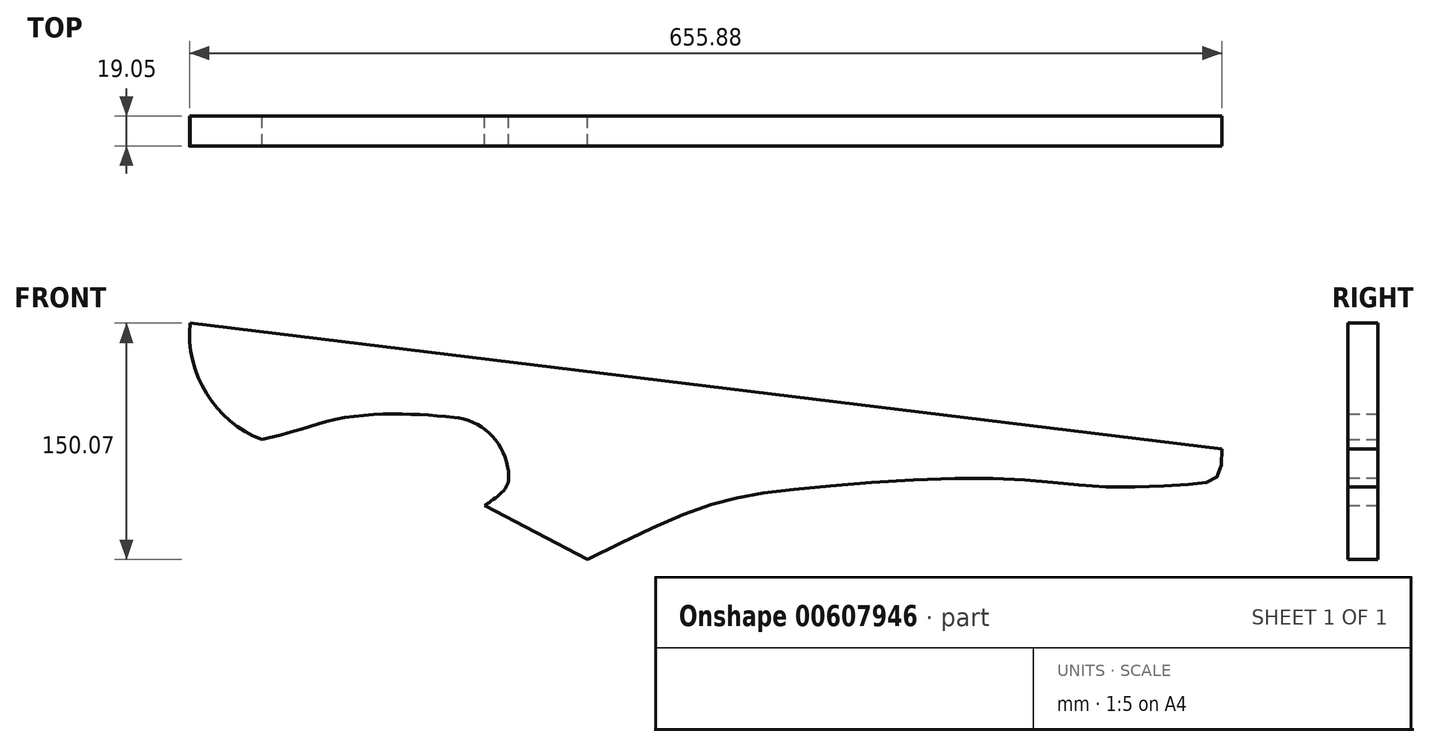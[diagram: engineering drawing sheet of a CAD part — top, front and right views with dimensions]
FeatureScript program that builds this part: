
annotation { "Feature Type Name" : "Feature", "Feature Type Description" : "" }
export const myFeature = defineFeature(function(context is Context, id is Id, definition is map)
    precondition{}
    {
        {
            var Q0;
            Q0=qCreatedBy(makeId("Front.planeOp"),FACE);
            var sketch = newSketch(context, id + "F0", { "sketchPlane" : qUnion([Q0])});
            skLineSegment(sketch, "E0", {"start": v(-277.74, 223.26) * mm, "end": v(377.83, 143.5) * mm});
            skPoint(sketch, "E1.third.point", {"position": v(-154.98, 165.5) * mm});
            skArc(sketch, "E2", {"start": v(-232.24, 149.4) * mm, "mid": v(-232.14, 149.35) * mm, "end": v(-232.03, 149.3) * mm});
            skArc(sketch, "E3", {"start": v(-277.74, 223.26) * mm, "mid": v(-267.34, 178.72) * mm, "end": v(-232.24, 149.4) * mm});
            skArc(sketch, "E4", {"start": v(-75.88, 131.97) * mm, "mid": v(-87.72, 153.44) * mm, "end": v(-110.1, 163.47) * mm});
            skFitSpline(sketch, "E5", {"points": [v(-232.03, 149.3) * mm, v(-212.68, 154.23) * mm, v(-182.77, 162.7) * mm, v(-142.55, 165.5) * mm, v(-110.1, 163.47) * mm], "startDerivative": vector(91.7, 21) * mm, "endDerivative": vector(120.47, -13) * mm});
            skFitSpline(sketch, "E6", {"points": [v(-75.88, 131.97) * mm, v(-77.7, 118) * mm, v(-90.46, 107.58) * mm], "startDerivative": vector(5.3, -30.31) * mm, "endDerivative": vector(-5.35, -3.75) * mm});
            skPoint(sketch, "E7.third.point", {"position": v(207.12, 2009.61) * mm});
            skFitSpline(sketch, "E8", {"points": [v(91.03, -76.58) * mm, v(51.5, -81.93) * mm, v(-9.28, -70.04) * mm, v(-67.9, -48.96) * mm, v(-99.5, -32.48) * mm, v(-109.24, -12.03) * mm, v(-100.85, 11.47) * mm, v(-84.66, 36.06) * mm, v(-46.79, 61.65) * mm, v(41.34, 103.83) * mm, v(105.63, 117.62) * mm, v(235.57, 124.62) * mm, v(301, 119.45) * mm, v(360.96, 121.33) * mm, v(375.02, 125.92) * mm, v(377.83, 143.5) * mm], "startDerivative": vector(-611.1, -137.7) * mm, "endDerivative": vector(6.45, 510.82) * mm});
            skLineSegment(sketch, "E9", {"start": v(-25.04, 73.2) * mm, "end": v(-90.46, 107.58) * mm});
            skSolve(sketch);
        }
        {
            var Q0;
            Q0 = qSketchRegion(id + "F0", true);
            extrude(context, id + "F1", {"entities" : qUnion([Q0]), "depth" : 19.05 * mm, "offsetDistance" : 25.4 * mm});
        }
    });
